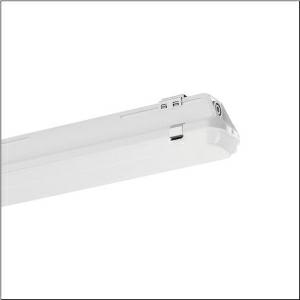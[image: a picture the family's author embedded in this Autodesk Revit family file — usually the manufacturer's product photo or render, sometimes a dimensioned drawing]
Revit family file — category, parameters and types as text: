
# Revit family: monsun_r__21_emergency_51fb10dp487b3h_7346
name_source: partatom
category: Lighting Fixtures
units: mm (PartAtom-declared; Revit-internal decimal feet)

## family parameters
Cut with Voids When Loaded = No
Host = Face
Light Source = No
Part Type = Normal
Room Calculation Point = No
Round Connector Dimension = Use Diameter
Shared = No

## types (1)
- --- (1 x LED, 8090 lm, 57.2 W, 4000K)
    Apparent Load = 57 VA
    CIE Flux Codes = 47 77 93 94 100
    Color Rendering = 80
    Color Temperature = 4000K
    Default Elevation = 1800 mm
    Description = Monsun® 21 emergency, damp-proof luminaire, chain hanger, primary optical cover: enclosure, of PMMA, light emission: direct distribution, primary light characteristic: symmetric, installation type: vertical mounting, horizontal mounting, surface-mounted, suspended mounting, LED, rated luminous flux: 8.090lm, luminous efficacy: 141lm/W, light colour: 840, colour temperature: 4000K, control gear: ECG DALI, with terminal, 5+3-pole, max. 2.5mm², mains connection: 220..240V, AC, 50/60Hz, rated input power: 57W, control gear: single battery element, battery: NiCd, 4,5Ah, mains connection: 230V, housing, of glass-fibre reinforced polyester, uncoated, bright grey, length: 1.590mm, width: 90mm, height: 88mm, clip for enclosure, of stainless steel (V2A), ceiling mounting element, of stainless steel (V2A), chain hanger, of stainless steel (V2A), protection rating (complete): IP66, insulation class (complete): insulation class I (protective earthing), certification: CE, UKCA, protection symbol: D, impact resistance: IK04, permissible operating ambient temperature: +5..+25°C, standard: EN 60598-2-1, EN 50419, EN 60598-2-22, corresponds to IFS (International Featured Standards) requirements for safety and quality in the food industry, for indoor or canopied outdoor use, no direct snow, no direct sun, no direct rain, packaging unit: 1 piece
    Height = 89 mm
    Lamp = 1 x LED
    Lamp Light Flux = 8090 lm
    Lamp Power = 57.2 W
    Lamp count = 1
    Length = 1590 mm
    Luminous efficacy = 141 lm/W
    Manufacturer = Siteco
    ModVariant = No
    Model = 51FB10DP487B3H
    Mounting Place = Ceiling
    Mounting Type = Pendant
    Number of Poles = 1
    OnlyDefault = Yes
    Power Factor = 1
    Product Name = Monsun® 21 emergency
    Product group = damp-proof luminaire | ceiling pendant
    ProductGroupID = 908
    Protection Class = Protection class I
    Protection Degree = IP 66
    RLX_Detail_Level = 1
    RlxData = <blob elided: 92597 chars, md5=931acd62>
    Socket = socket
    Standby Power = 0 W
    System Light Flux = 8090 lm
    System Power = 57 W
    Type Comments = factory setting: luminous flux: 100 % | dim-lin: 254 | 358 mA
    Type Image = l_1006717.jpg
    URL = http://relux.com
    VarID = @adj_124831
    Voltage = 0 V
    Weight = 0.00 kg
    Width = 90 mm

## geometry (parser evidence)
native form markers: Blend x4, Sweep x12
no freeform markers — native parametric forms only
